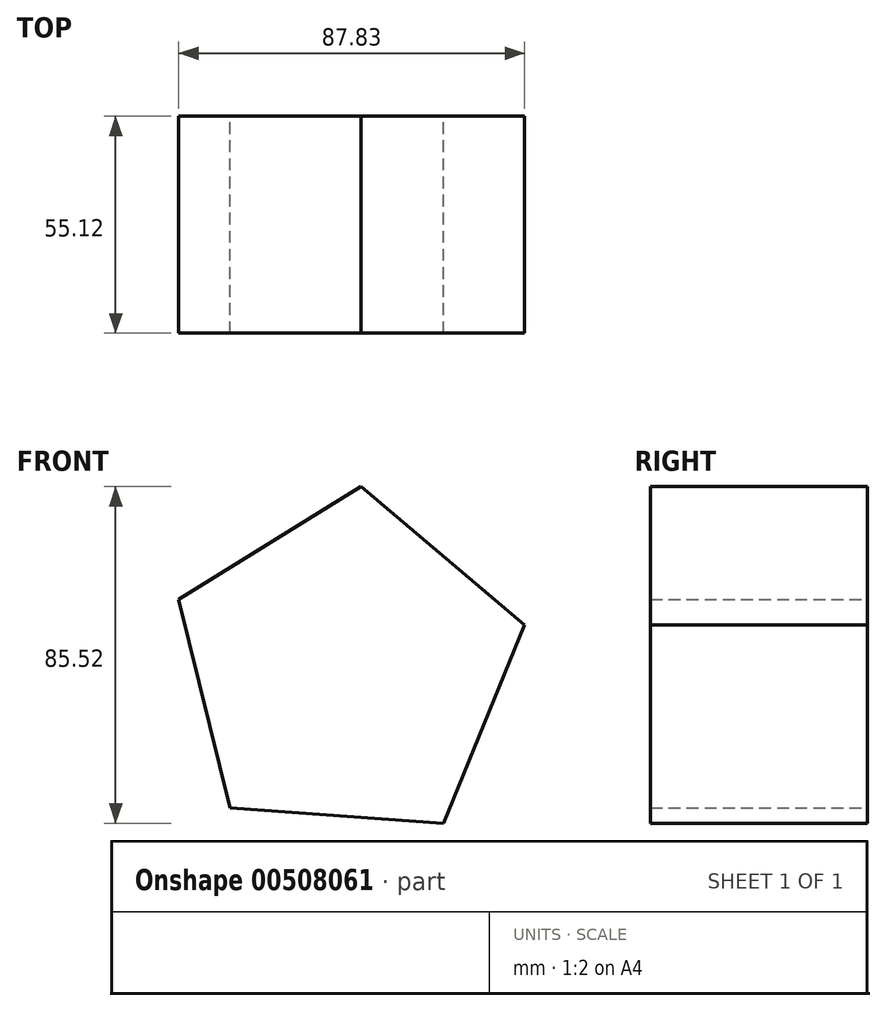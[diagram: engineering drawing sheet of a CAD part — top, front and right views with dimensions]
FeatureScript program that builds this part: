
annotation { "Feature Type Name" : "Feature", "Feature Type Description" : "" }
export const myFeature = defineFeature(function(context is Context, id is Id, definition is map)
    precondition{}
    {
        {
            var Q0;
            Q0=qCreatedBy(makeId("Front.planeOp"),FACE);
            var sketch = newSketch(context, id + "F0", { "sketchPlane" : qUnion([Q0])});
            skCircle(sketch, "E0.cCircle", {"center": v(0, 0) * mm, "radius": 37.46 * mm, "construction": true});
            skLineSegment(sketch, "E0.0", {"start": v(44.96, 11.06) * mm, "end": v(24.41, -39.34) * mm});
            skLineSegment(sketch, "E0.1", {"start": v(24.41, -39.34) * mm, "end": v(-29.87, -35.38) * mm});
            skLineSegment(sketch, "E0.2", {"start": v(-29.87, -35.38) * mm, "end": v(-42.87, 17.47) * mm});
            skLineSegment(sketch, "E0.3", {"start": v(-42.87, 17.47) * mm, "end": v(3.37, 46.18) * mm});
            skLineSegment(sketch, "E0.4", {"start": v(3.37, 46.18) * mm, "end": v(44.96, 11.06) * mm});
            skPoint(sketch, "E0.0.midPoint", {"position": v(34.69, -14.14) * mm});
            skSolve(sketch);
        }
        {
            var Q0;
            Q0=makeQuery(id+"F0.imprint","IMPRINT",FACE,{"disambiguationData":[TD([[makeQuery(id+"F0.imprint","IMPRINT",EDGE,{"derivedFrom":sQuery(id+"F0.wireOp",EDGE,"E0.0")}),-1.0]])]});
            extrude(context, id + "F1", {"entities" : qUnion([Q0]), "depth" : 55.12 * mm});
        }
    });
